# Revit family: iwszpm
name_source: partatom
category: Communication Devices
revit_build: Autodesk Revit 2014 (Build: 20130308_1515(x64)
units: mm (PartAtom-declared; Revit-internal decimal feet)

## types (1)
- iwszpm
    Assembly Code = D5090
    Black = Paint - Hubbell - Carbon Black
    Default Elevation = 48 "
    Description = The IWSZP3P is an automatic passive infrared wall switch occupancy sensor
that provides excellent energy savings as well as reliable motion detection.
The sensors’ low profile housing design provides the perfect wall switch for
applications including private offices, conference rooms, break rooms, lounges
and storage areas.
    Features = Zero Arc Point Switching
• No minimum load requirement
• Adjustable time delay and sensitivity
• Built-in photocell
• Walk test indicator
• Dual 120/277VAC operation
• UL and cUL listed
• Five-year limited warranty
• 120-277 Vac
    Height = 4.5 "
    Manufacturer = Hubbell Control Solutions
    Model = Manual On/ Auto OFF Passive Infrared Wall Switch Sensor
    Product Documentation Link = https://hubbellcdn.com
    Product Page URL = https://www.hubbell.com
    Standby Power = 120 or 277VAC, 60 Hz
    Type Comments = Manual On/ Auto OFF Passive Infrared Wall Switch Sensor
    URL = https://www.hubbell.com
    Warranty = 5-Years Warranty
    White = Paint - Hubbell - Matte White
    Width = 2.75 "

## geometry (parser evidence)
native form markers: Sweep x1
no freeform markers — native parametric forms only
